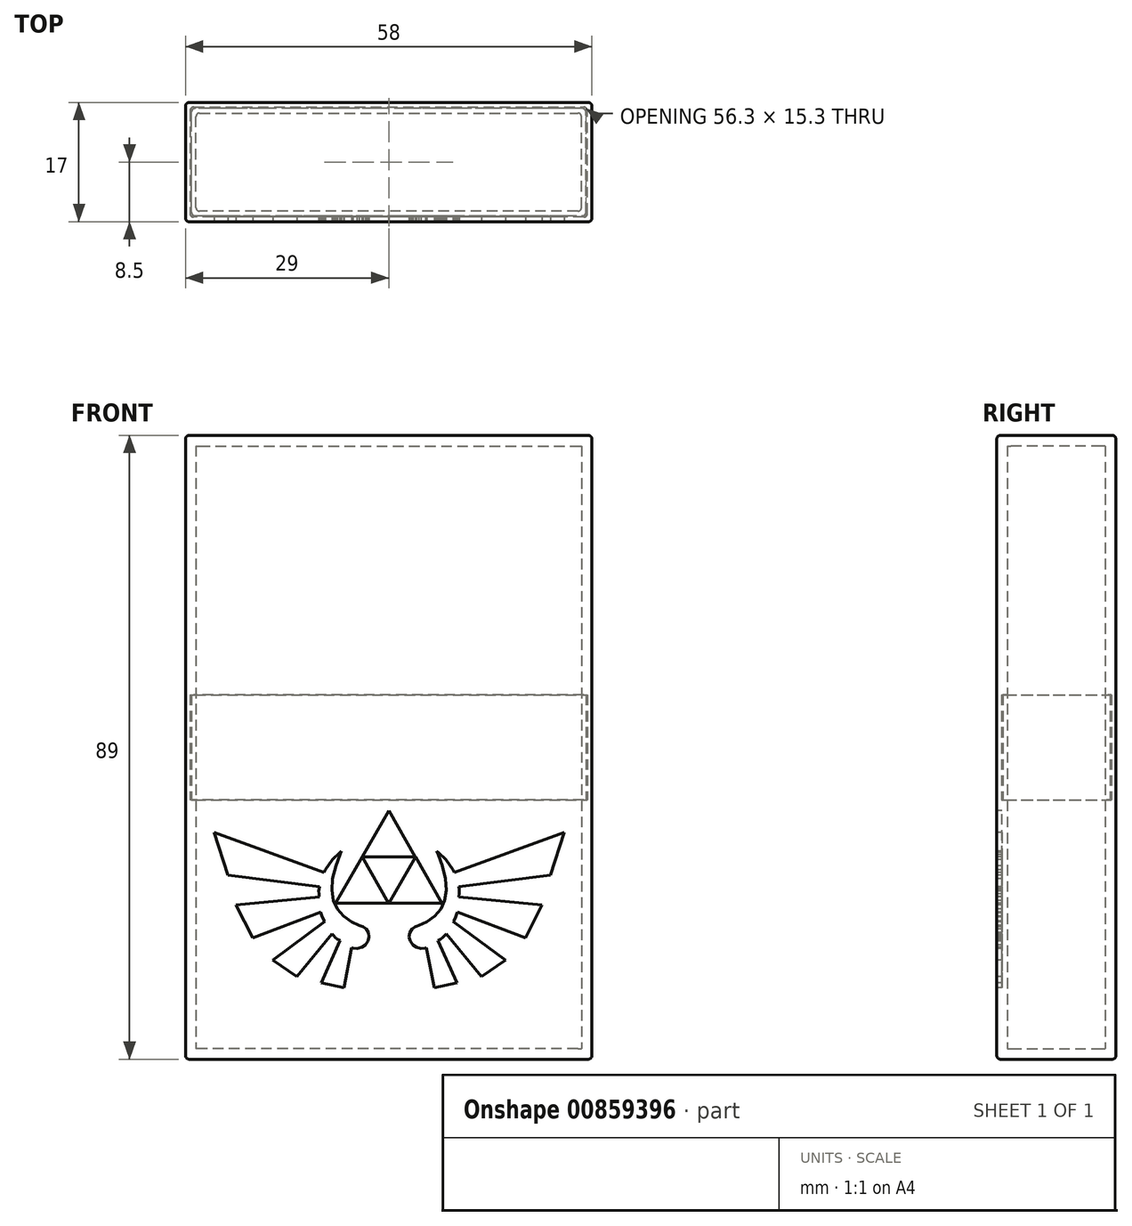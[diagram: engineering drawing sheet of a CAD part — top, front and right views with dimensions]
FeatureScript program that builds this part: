
annotation { "Feature Type Name" : "Feature", "Feature Type Description" : "" }
export const myFeature = defineFeature(function(context is Context, id is Id, definition is map)
    precondition{}
    {
        {
            assignVariable(context, id + "F0", {"name" : "wall_thickness", "anyValue" : 1.5});
        }
        {
            var Q0;
            Q0=qCreatedBy(makeId("Top.planeOp"),FACE);
            var sketch = newSketch(context, id + "F1", { "sketchPlane" : qUnion([Q0])});
            skLineSegment(sketch, "E0", {"start": v(-29, 0) * mm, "end": v(-29, 8.5) * mm});
            skLineSegment(sketch, "E1", {"start": v(-29, 8.5) * mm, "end": v(0, 8.5) * mm});
            skLineSegment(sketch, "E2.MirrorCS", {"start": v(29, 8.5) * mm, "end": v(0, 8.5) * mm});
            skLineSegment(sketch, "E3.MirrorCS", {"start": v(29, 0) * mm, "end": v(29, 8.5) * mm});
            skLineSegment(sketch, "E4.MirrorCS", {"start": v(29, 0) * mm, "end": v(29, -8.5) * mm});
            skLineSegment(sketch, "E5.MirrorCS", {"start": v(29, -8.5) * mm, "end": v(0, -8.5) * mm});
            skLineSegment(sketch, "E6.MirrorCS", {"start": v(-29, -8.5) * mm, "end": v(0, -8.5) * mm});
            skLineSegment(sketch, "E7.MirrorCS", {"start": v(-29, 0) * mm, "end": v(-29, -8.5) * mm});
            skSolve(sketch);
        }
        {
            assignVariable(context, id + "F2", {"name" : "inside_height", "anyValue" : 86});
        }
        {
            var Q0;
            Q0=makeQuery(id+"F1.imprint","IMPRINT",FACE,{"disambiguationData":[TD([[makeQuery(id+"F1.imprint","IMPRINT",EDGE,{"derivedFrom":sQuery(id+"F1.wireOp",EDGE,"E0")}),-1.0]])]});
            extrude(context, id + "F3", {"entities" : qUnion([Q0]), "depth" : (getVariable(context, 'wall_thickness')) * mm, "offsetDistance" : 25 * mm});
        }
        {
            var Q0;
            Q0=makeQuery(id+"F3.opExtrude","CAP_FACE",FACE,{"disambiguationData":[OSD([sQuery(id+"F1.wireOp",EDGE,"E0"),sQuery(id+"F1.wireOp",EDGE,"E1"),sQuery(id+"F1.wireOp",EDGE,"E2.MirrorCS"),sQuery(id+"F1.wireOp",EDGE,"E3.MirrorCS"),sQuery(id+"F1.wireOp",EDGE,"E4.MirrorCS"),sQuery(id+"F1.wireOp",EDGE,"E5.MirrorCS"),sQuery(id+"F1.wireOp",EDGE,"E6.MirrorCS"),sQuery(id+"F1.wireOp",EDGE,"E7.MirrorCS")])],"isStart":false});
            var sketch = newSketch(context, id + "F4", { "sketchPlane" : qUnion([Q0])});
            skLineSegment(sketch, "E8", {"start": v(-27.5, 0) * mm, "end": v(-27.5, 7) * mm});
            skLineSegment(sketch, "E9", {"start": v(-27.5, 7) * mm, "end": v(0, 7) * mm});
            skLineSegment(sketch, "E10.MirrorCS", {"start": v(27.5, 0) * mm, "end": v(27.5, 7) * mm});
            skLineSegment(sketch, "E11.MirrorCS", {"start": v(27.5, 7) * mm, "end": v(0, 7) * mm});
            skLineSegment(sketch, "E12.MirrorCS", {"start": v(27.5, 0) * mm, "end": v(27.5, -7) * mm});
            skLineSegment(sketch, "E13.MirrorCS", {"start": v(27.5, -7) * mm, "end": v(0, -7) * mm});
            skLineSegment(sketch, "E14.MirrorCS", {"start": v(-27.5, -7) * mm, "end": v(0, -7) * mm});
            skLineSegment(sketch, "E15.MirrorCS", {"start": v(-27.5, 0) * mm, "end": v(-27.5, -7) * mm});
            skSolve(sketch);
        }
        {
            assignVariable(context, id + "F5", {"name" : "mate_height", "anyValue" : 15});
        }
        {
            var Q0;
            Q0=makeQuery(id+"F4.imprint","IMPRINT",FACE,{"disambiguationData":[TD([[makeQuery(id+"F4.imprint","IMPRINT",EDGE,{"derivedFrom":sQuery(id+"F4.wireOp",EDGE,"E8")}),1.0]])]});
            extrude(context, id + "F6", {"entities" : qUnion([Q0]), "operationType" : NewBodyOperationType.ADD, "depth" : (getVariable(context, 'inside_height') - getVariable(context, 'mate_height')) / 2 * mm, "offsetDistance" : 25 * mm});
        }
        {
            var Q0;
            Q0=makeQuery(id+"F6.opExtrude","CAP_FACE",FACE,{"disambiguationData":[OSD([sQuery(id+"F1.wireOp",EDGE,"E0"),sQuery(id+"F1.wireOp",EDGE,"E1"),sQuery(id+"F1.wireOp",EDGE,"E2.MirrorCS"),sQuery(id+"F1.wireOp",EDGE,"E3.MirrorCS"),sQuery(id+"F1.wireOp",EDGE,"E4.MirrorCS"),sQuery(id+"F1.wireOp",EDGE,"E5.MirrorCS"),sQuery(id+"F1.wireOp",EDGE,"E6.MirrorCS"),sQuery(id+"F1.wireOp",EDGE,"E7.MirrorCS"),sQuery(id+"F4.wireOp",EDGE,"E8"),sQuery(id+"F4.wireOp",EDGE,"E9"),sQuery(id+"F4.wireOp",EDGE,"E10.MirrorCS"),sQuery(id+"F4.wireOp",EDGE,"E11.MirrorCS"),sQuery(id+"F4.wireOp",EDGE,"E12.MirrorCS"),sQuery(id+"F4.wireOp",EDGE,"E13.MirrorCS"),sQuery(id+"F4.wireOp",EDGE,"E14.MirrorCS"),sQuery(id+"F4.wireOp",EDGE,"E15.MirrorCS")])],"isStart":false});
            var sketch = newSketch(context, id + "F7", { "sketchPlane" : qUnion([Q0])});
            skLineSegment(sketch, "E16", {"start": v(-28.15, 0) * mm, "end": v(-28.15, 7.65) * mm});
            skPoint(sketch, "E16.startSnap0", {"position": v(-29, 0) * mm});
            skLineSegment(sketch, "E17", {"start": v(-28.15, 7.65) * mm, "end": v(0, 7.65) * mm});
            skLineSegment(sketch, "E18.MirrorCS", {"start": v(28.15, 7.65) * mm, "end": v(0, 7.65) * mm});
            skLineSegment(sketch, "E19.MirrorCS", {"start": v(28.15, 0) * mm, "end": v(28.15, 7.65) * mm});
            skLineSegment(sketch, "E20.MirrorCS", {"start": v(-28.15, -7.65) * mm, "end": v(0, -7.65) * mm});
            skLineSegment(sketch, "E21.MirrorCS", {"start": v(28.15, -7.65) * mm, "end": v(0, -7.65) * mm});
            skLineSegment(sketch, "E22.MirrorCS", {"start": v(28.15, 0) * mm, "end": v(28.15, -7.65) * mm});
            skLineSegment(sketch, "E23.MirrorCS", {"start": v(-28.15, 0) * mm, "end": v(-28.15, -7.65) * mm});
            skSolve(sketch);
        }
        {
            var Q0;
            Q0=makeQuery(id+"F6.opExtrude","CAP_FACE",FACE,{"disambiguationData":[OSD([sQuery(id+"F1.wireOp",EDGE,"E0"),sQuery(id+"F1.wireOp",EDGE,"E1"),sQuery(id+"F1.wireOp",EDGE,"E2.MirrorCS"),sQuery(id+"F1.wireOp",EDGE,"E3.MirrorCS"),sQuery(id+"F1.wireOp",EDGE,"E4.MirrorCS"),sQuery(id+"F1.wireOp",EDGE,"E5.MirrorCS"),sQuery(id+"F1.wireOp",EDGE,"E6.MirrorCS"),sQuery(id+"F1.wireOp",EDGE,"E7.MirrorCS"),sQuery(id+"F4.wireOp",EDGE,"E8"),sQuery(id+"F4.wireOp",EDGE,"E9"),sQuery(id+"F4.wireOp",EDGE,"E10.MirrorCS"),sQuery(id+"F4.wireOp",EDGE,"E11.MirrorCS"),sQuery(id+"F4.wireOp",EDGE,"E12.MirrorCS"),sQuery(id+"F4.wireOp",EDGE,"E13.MirrorCS"),sQuery(id+"F4.wireOp",EDGE,"E14.MirrorCS"),sQuery(id+"F4.wireOp",EDGE,"E15.MirrorCS")])],"isStart":false});
            var sketch = newSketch(context, id + "F8", { "sketchPlane" : qUnion([Q0])});
            skLineSegment(sketch, "E24", {"start": v(-28.35, 0) * mm, "end": v(-28.35, 7.85) * mm});
            skPoint(sketch, "E24.startSnap0", {"position": v(-29, 0) * mm});
            skLineSegment(sketch, "E25", {"start": v(-28.35, 7.85) * mm, "end": v(0, 7.85) * mm});
            skLineSegment(sketch, "E26.MirrorCS", {"start": v(28.35, 7.85) * mm, "end": v(0, 7.85) * mm});
            skLineSegment(sketch, "E27.MirrorCS", {"start": v(28.35, 0) * mm, "end": v(28.35, 7.85) * mm});
            skLineSegment(sketch, "E28.MirrorCS", {"start": v(-28.35, -7.85) * mm, "end": v(0, -7.85) * mm});
            skLineSegment(sketch, "E29.MirrorCS", {"start": v(-28.35, 0) * mm, "end": v(-28.35, -7.85) * mm});
            skLineSegment(sketch, "E30.MirrorCS", {"start": v(28.35, -7.85) * mm, "end": v(0, -7.85) * mm});
            skLineSegment(sketch, "E31.MirrorCS", {"start": v(28.35, 0) * mm, "end": v(28.35, -7.85) * mm});
            skSolve(sketch);
        }
        {
            var Q0;
            Q0=makeQuery(id+"F7.imprint","IMPRINT",FACE,{"disambiguationData":[TD([[makeQuery(id+"F7.imprint","IMPRINT",EDGE,{"derivedFrom":sQuery(id+"F7.wireOp",EDGE,"E16")}),-1.0]])]});
            extrude(context, id + "F9", {"entities" : qUnion([Q0]), "operationType" : NewBodyOperationType.ADD, "depth" : (getVariable(context, 'mate_height')) * mm, "offsetDistance" : 25 * mm});
        }
        {
            var Q0;
            Q0=makeQuery(id+"F8.imprint","IMPRINT",FACE,{"disambiguationData":[TD([[makeQuery(id+"F8.imprint","IMPRINT",EDGE,{"derivedFrom":sQuery(id+"F8.wireOp",EDGE,"E24")}),1.0]])]});
            var Q1;
            Q1=makeQuery(id+"F9.opExtrude","CAP_FACE",FACE,{"disambiguationData":[OSD([sQuery(id+"F4.wireOp",EDGE,"E8"),sQuery(id+"F4.wireOp",EDGE,"E9"),sQuery(id+"F4.wireOp",EDGE,"E10.MirrorCS"),sQuery(id+"F4.wireOp",EDGE,"E11.MirrorCS"),sQuery(id+"F4.wireOp",EDGE,"E12.MirrorCS"),sQuery(id+"F4.wireOp",EDGE,"E13.MirrorCS"),sQuery(id+"F4.wireOp",EDGE,"E14.MirrorCS"),sQuery(id+"F4.wireOp",EDGE,"E15.MirrorCS"),sQuery(id+"F7.wireOp",EDGE,"E16"),sQuery(id+"F7.wireOp",EDGE,"E17"),sQuery(id+"F7.wireOp",EDGE,"E18.MirrorCS"),sQuery(id+"F7.wireOp",EDGE,"E19.MirrorCS"),sQuery(id+"F7.wireOp",EDGE,"E20.MirrorCS"),sQuery(id+"F7.wireOp",EDGE,"E21.MirrorCS"),sQuery(id+"F7.wireOp",EDGE,"E22.MirrorCS"),sQuery(id+"F7.wireOp",EDGE,"E23.MirrorCS")])],"isStart":false});
            extrude(context, id + "F10", {"entities" : qUnion([Q0]), "endBound" : BoundingType.UP_TO_SURFACE, "depth" : 25 * mm, "endBoundEntityFace" : qUnion([Q1]), "offsetDistance" : 25 * mm});
        }
        {
            var Q0;
            Q0=makeQuery(id+"F10.opExtrude","CAP_FACE",FACE,{"disambiguationData":[OSD([sQuery(id+"F1.wireOp",EDGE,"E0"),sQuery(id+"F1.wireOp",EDGE,"E1"),sQuery(id+"F1.wireOp",EDGE,"E2.MirrorCS"),sQuery(id+"F1.wireOp",EDGE,"E3.MirrorCS"),sQuery(id+"F1.wireOp",EDGE,"E4.MirrorCS"),sQuery(id+"F1.wireOp",EDGE,"E5.MirrorCS"),sQuery(id+"F1.wireOp",EDGE,"E6.MirrorCS"),sQuery(id+"F1.wireOp",EDGE,"E7.MirrorCS"),sQuery(id+"F8.wireOp",EDGE,"E24"),sQuery(id+"F8.wireOp",EDGE,"E25"),sQuery(id+"F8.wireOp",EDGE,"E26.MirrorCS"),sQuery(id+"F8.wireOp",EDGE,"E27.MirrorCS"),sQuery(id+"F8.wireOp",EDGE,"E28.MirrorCS"),sQuery(id+"F8.wireOp",EDGE,"E29.MirrorCS"),sQuery(id+"F8.wireOp",EDGE,"E30.MirrorCS"),sQuery(id+"F8.wireOp",EDGE,"E31.MirrorCS")])],"isStart":false});
            var sketch = newSketch(context, id + "F11", { "sketchPlane" : qUnion([Q0])});
            skLineSegment(sketch, "E32.bottom", {"start": v(-29, 8.5) * mm, "end": v(29, 8.5) * mm});
            skLineSegment(sketch, "E32.top", {"start": v(-29, -8.5) * mm, "end": v(29, -8.5) * mm});
            skLineSegment(sketch, "E32.left", {"start": v(-29, 8.5) * mm, "end": v(-29, -8.5) * mm});
            skLineSegment(sketch, "E32.right", {"start": v(29, 8.5) * mm, "end": v(29, -8.5) * mm});
            skLineSegment(sketch, "E33.bottom", {"start": v(-27.5, 7) * mm, "end": v(27.5, 7) * mm});
            skLineSegment(sketch, "E33.top", {"start": v(-27.5, -7) * mm, "end": v(27.5, -7) * mm});
            skLineSegment(sketch, "E33.left", {"start": v(-27.5, 7) * mm, "end": v(-27.5, -7) * mm});
            skLineSegment(sketch, "E33.right", {"start": v(27.5, 7) * mm, "end": v(27.5, -7) * mm});
            skSolve(sketch);
        }
        {
            var Q0;
            Q0 = qSketchRegion(id + "F11", true);
            extrude(context, id + "F12", {"entities" : qUnion([Q0]), "operationType" : NewBodyOperationType.ADD, "depth" : (getVariable(context, 'inside_height') - getVariable(context, 'mate_height')) / 2 * mm, "offsetDistance" : 25 * mm});
        }
        {
            var Q0;
            Q0=makeQuery(id+"F12.opExtrude","CAP_FACE",FACE,{"disambiguationData":[OSD([sQuery(id+"F11.wireOp",EDGE,"E32.bottom"),sQuery(id+"F11.wireOp",EDGE,"E32.top"),sQuery(id+"F11.wireOp",EDGE,"E32.left"),sQuery(id+"F11.wireOp",EDGE,"E32.right"),sQuery(id+"F11.wireOp",EDGE,"E33.bottom"),sQuery(id+"F11.wireOp",EDGE,"E33.top"),sQuery(id+"F11.wireOp",EDGE,"E33.left"),sQuery(id+"F11.wireOp",EDGE,"E33.right")])],"isStart":false});
            var sketch = newSketch(context, id + "F13", { "sketchPlane" : qUnion([Q0])});
            skLineSegment(sketch, "E34.bottom", {"start": v(-29, 8.5) * mm, "end": v(29, 8.5) * mm});
            skLineSegment(sketch, "E34.top", {"start": v(-29, -8.5) * mm, "end": v(29, -8.5) * mm});
            skLineSegment(sketch, "E34.left", {"start": v(-29, 8.5) * mm, "end": v(-29, -8.5) * mm});
            skLineSegment(sketch, "E34.right", {"start": v(29, 8.5) * mm, "end": v(29, -8.5) * mm});
            skSolve(sketch);
        }
        {
            var Q0;
            Q0 = qSketchRegion(id + "F13", true);
            extrude(context, id + "F14", {"entities" : qUnion([Q0]), "operationType" : NewBodyOperationType.ADD, "depth" : (getVariable(context, 'wall_thickness')) * mm, "offsetDistance" : 25 * mm});
        }
        {
            var Q0;
            {var subQ0=sQuery(id+"F1.wireOp",EDGE,"E7.MirrorCS");var subQ1=sQuery(id+"F1.wireOp",EDGE,"E6.MirrorCS");Q0=makeQuery(id+"F6.boolean.opBoolean","MERGE",EDGE,{"derivedFrom":[makeQuery(id+"F3.opExtrude","SWEPT_EDGE",EDGE,{"disambiguationData":[OSD([subQ1,subQ0])]}),makeQuery(id+"F6.opExtrude","SWEPT_EDGE",EDGE,{"disambiguationData":[OSD([sQuery(id+"F1.wireOp",EDGE,"E0"),sQuery(id+"F1.wireOp",EDGE,"E5.MirrorCS"),subQ1,subQ0])]})]});}
            var Q1;
            {var subQ0=sQuery(id+"F1.wireOp",EDGE,"E1");var subQ1=sQuery(id+"F1.wireOp",EDGE,"E0");Q1=makeQuery(id+"F6.boolean.opBoolean","MERGE",EDGE,{"derivedFrom":[makeQuery(id+"F3.opExtrude","SWEPT_EDGE",EDGE,{"disambiguationData":[OSD([subQ1,subQ0])]}),makeQuery(id+"F6.opExtrude","SWEPT_EDGE",EDGE,{"disambiguationData":[OSD([subQ1,subQ0,sQuery(id+"F1.wireOp",EDGE,"E2.MirrorCS"),sQuery(id+"F1.wireOp",EDGE,"E7.MirrorCS")])]})]});}
            var Q2;
            {var subQ0=sQuery(id+"F1.wireOp",EDGE,"E3.MirrorCS");var subQ1=sQuery(id+"F1.wireOp",EDGE,"E2.MirrorCS");Q2=makeQuery(id+"F6.boolean.opBoolean","MERGE",EDGE,{"derivedFrom":[makeQuery(id+"F3.opExtrude","SWEPT_EDGE",EDGE,{"disambiguationData":[OSD([subQ1,subQ0])]}),makeQuery(id+"F6.opExtrude","SWEPT_EDGE",EDGE,{"disambiguationData":[OSD([sQuery(id+"F1.wireOp",EDGE,"E1"),subQ1,subQ0,sQuery(id+"F1.wireOp",EDGE,"E4.MirrorCS")])]})]});}
            var Q3;
            {var subQ0=sQuery(id+"F1.wireOp",EDGE,"E5.MirrorCS");var subQ1=sQuery(id+"F1.wireOp",EDGE,"E4.MirrorCS");Q3=makeQuery(id+"F6.boolean.opBoolean","MERGE",EDGE,{"derivedFrom":[makeQuery(id+"F3.opExtrude","SWEPT_EDGE",EDGE,{"disambiguationData":[OSD([subQ1,subQ0])]}),makeQuery(id+"F6.opExtrude","SWEPT_EDGE",EDGE,{"disambiguationData":[OSD([sQuery(id+"F1.wireOp",EDGE,"E3.MirrorCS"),subQ1,subQ0,sQuery(id+"F1.wireOp",EDGE,"E6.MirrorCS")])]})]});}
            var Q4;
            Q4=makeQuery(id+"F9.opExtrude","SWEPT_EDGE",EDGE,{"disambiguationData":[OSD([sQuery(id+"F7.wireOp",EDGE,"E21.MirrorCS"),sQuery(id+"F7.wireOp",EDGE,"E22.MirrorCS")])]});
            var Q5;
            Q5=makeQuery(id+"F9.opExtrude","SWEPT_EDGE",EDGE,{"disambiguationData":[OSD([sQuery(id+"F7.wireOp",EDGE,"E18.MirrorCS"),sQuery(id+"F7.wireOp",EDGE,"E19.MirrorCS")])]});
            var Q6;
            Q6=makeQuery(id+"F9.opExtrude","SWEPT_EDGE",EDGE,{"disambiguationData":[OSD([sQuery(id+"F7.wireOp",EDGE,"E16"),sQuery(id+"F7.wireOp",EDGE,"E17")])]});
            var Q7;
            Q7=makeQuery(id+"F9.opExtrude","SWEPT_EDGE",EDGE,{"disambiguationData":[OSD([sQuery(id+"F7.wireOp",EDGE,"E20.MirrorCS"),sQuery(id+"F7.wireOp",EDGE,"E23.MirrorCS")])]});
            var Q8;
            {var subQ0=sQuery(id+"F4.wireOp",EDGE,"E11.MirrorCS");var subQ1=sQuery(id+"F4.wireOp",EDGE,"E10.MirrorCS");Q8=makeQuery(id+"F9.boolean.opBoolean","MERGE",EDGE,{"derivedFrom":[makeQuery(id+"F6.opExtrude","SWEPT_EDGE",EDGE,{"disambiguationData":[OSD([subQ1,subQ0])]}),makeQuery(id+"F9.opExtrude","SWEPT_EDGE",EDGE,{"disambiguationData":[OSD([sQuery(id+"F4.wireOp",EDGE,"E9"),subQ1,subQ0,sQuery(id+"F4.wireOp",EDGE,"E12.MirrorCS")])]})]});}
            var Q9;
            {var subQ0=sQuery(id+"F4.wireOp",EDGE,"E9");var subQ1=sQuery(id+"F4.wireOp",EDGE,"E8");Q9=makeQuery(id+"F9.boolean.opBoolean","MERGE",EDGE,{"derivedFrom":[makeQuery(id+"F6.opExtrude","SWEPT_EDGE",EDGE,{"disambiguationData":[OSD([subQ1,subQ0])]}),makeQuery(id+"F9.opExtrude","SWEPT_EDGE",EDGE,{"disambiguationData":[OSD([subQ1,subQ0,sQuery(id+"F4.wireOp",EDGE,"E11.MirrorCS"),sQuery(id+"F4.wireOp",EDGE,"E15.MirrorCS")])]})]});}
            var Q10;
            {var subQ0=sQuery(id+"F4.wireOp",EDGE,"E15.MirrorCS");var subQ1=sQuery(id+"F4.wireOp",EDGE,"E14.MirrorCS");Q10=makeQuery(id+"F9.boolean.opBoolean","MERGE",EDGE,{"derivedFrom":[makeQuery(id+"F6.opExtrude","SWEPT_EDGE",EDGE,{"disambiguationData":[OSD([subQ1,subQ0])]}),makeQuery(id+"F9.opExtrude","SWEPT_EDGE",EDGE,{"disambiguationData":[OSD([sQuery(id+"F4.wireOp",EDGE,"E8"),sQuery(id+"F4.wireOp",EDGE,"E13.MirrorCS"),subQ1,subQ0])]})]});}
            var Q11;
            {var subQ0=sQuery(id+"F4.wireOp",EDGE,"E13.MirrorCS");var subQ1=sQuery(id+"F4.wireOp",EDGE,"E12.MirrorCS");Q11=makeQuery(id+"F9.boolean.opBoolean","MERGE",EDGE,{"derivedFrom":[makeQuery(id+"F6.opExtrude","SWEPT_EDGE",EDGE,{"disambiguationData":[OSD([subQ1,subQ0])]}),makeQuery(id+"F9.opExtrude","SWEPT_EDGE",EDGE,{"disambiguationData":[OSD([sQuery(id+"F4.wireOp",EDGE,"E10.MirrorCS"),subQ1,subQ0,sQuery(id+"F4.wireOp",EDGE,"E14.MirrorCS")])]})]});}
            var Q12;
            Q12=makeQuery(id+"F14.boolean.opBoolean","MERGE",EDGE,{"derivedFrom":[makeQuery(id+"F12.boolean.opBoolean","MERGE",EDGE,{"derivedFrom":[makeQuery(id+"F10.opExtrude","SWEPT_EDGE",EDGE,{"disambiguationData":[OSD([sQuery(id+"F1.wireOp",EDGE,"E0"),sQuery(id+"F1.wireOp",EDGE,"E5.MirrorCS"),sQuery(id+"F1.wireOp",EDGE,"E6.MirrorCS"),sQuery(id+"F1.wireOp",EDGE,"E7.MirrorCS")])]}),makeQuery(id+"F12.opExtrude","SWEPT_EDGE",EDGE,{"disambiguationData":[OSD([sQuery(id+"F11.wireOp",EDGE,"E32.top"),sQuery(id+"F11.wireOp",EDGE,"E32.left")])]})]}),makeQuery(id+"F14.opExtrude","SWEPT_EDGE",EDGE,{"disambiguationData":[OSD([sQuery(id+"F13.wireOp",EDGE,"E34.top"),sQuery(id+"F13.wireOp",EDGE,"E34.left")])]})]});
            var Q13;
            Q13=makeQuery(id+"F14.boolean.opBoolean","MERGE",EDGE,{"derivedFrom":[makeQuery(id+"F12.boolean.opBoolean","MERGE",EDGE,{"derivedFrom":[makeQuery(id+"F10.opExtrude","SWEPT_EDGE",EDGE,{"disambiguationData":[OSD([sQuery(id+"F1.wireOp",EDGE,"E0"),sQuery(id+"F1.wireOp",EDGE,"E1"),sQuery(id+"F1.wireOp",EDGE,"E2.MirrorCS"),sQuery(id+"F1.wireOp",EDGE,"E7.MirrorCS")])]}),makeQuery(id+"F12.opExtrude","SWEPT_EDGE",EDGE,{"disambiguationData":[OSD([sQuery(id+"F11.wireOp",EDGE,"E32.bottom"),sQuery(id+"F11.wireOp",EDGE,"E32.left")])]})]}),makeQuery(id+"F14.opExtrude","SWEPT_EDGE",EDGE,{"disambiguationData":[OSD([sQuery(id+"F13.wireOp",EDGE,"E34.bottom"),sQuery(id+"F13.wireOp",EDGE,"E34.left")])]})]});
            var Q14;
            Q14=makeQuery(id+"F14.boolean.opBoolean","MERGE",EDGE,{"derivedFrom":[makeQuery(id+"F12.boolean.opBoolean","MERGE",EDGE,{"derivedFrom":[makeQuery(id+"F10.opExtrude","SWEPT_EDGE",EDGE,{"disambiguationData":[OSD([sQuery(id+"F1.wireOp",EDGE,"E3.MirrorCS"),sQuery(id+"F1.wireOp",EDGE,"E4.MirrorCS"),sQuery(id+"F1.wireOp",EDGE,"E5.MirrorCS"),sQuery(id+"F1.wireOp",EDGE,"E6.MirrorCS")])]}),makeQuery(id+"F12.opExtrude","SWEPT_EDGE",EDGE,{"disambiguationData":[OSD([sQuery(id+"F11.wireOp",EDGE,"E32.top"),sQuery(id+"F11.wireOp",EDGE,"E32.right")])]})]}),makeQuery(id+"F14.opExtrude","SWEPT_EDGE",EDGE,{"disambiguationData":[OSD([sQuery(id+"F13.wireOp",EDGE,"E34.top"),sQuery(id+"F13.wireOp",EDGE,"E34.right")])]})]});
            var Q15;
            Q15=makeQuery(id+"F14.boolean.opBoolean","MERGE",EDGE,{"derivedFrom":[makeQuery(id+"F12.boolean.opBoolean","MERGE",EDGE,{"derivedFrom":[makeQuery(id+"F10.opExtrude","SWEPT_EDGE",EDGE,{"disambiguationData":[OSD([sQuery(id+"F1.wireOp",EDGE,"E1"),sQuery(id+"F1.wireOp",EDGE,"E2.MirrorCS"),sQuery(id+"F1.wireOp",EDGE,"E3.MirrorCS"),sQuery(id+"F1.wireOp",EDGE,"E4.MirrorCS")])]}),makeQuery(id+"F12.opExtrude","SWEPT_EDGE",EDGE,{"disambiguationData":[OSD([sQuery(id+"F11.wireOp",EDGE,"E32.bottom"),sQuery(id+"F11.wireOp",EDGE,"E32.right")])]})]}),makeQuery(id+"F14.opExtrude","SWEPT_EDGE",EDGE,{"disambiguationData":[OSD([sQuery(id+"F13.wireOp",EDGE,"E34.bottom"),sQuery(id+"F13.wireOp",EDGE,"E34.right")])]})]});
            var Q16;
            Q16=makeQuery(id+"F10.opExtrude","SWEPT_EDGE",EDGE,{"disambiguationData":[OSD([sQuery(id+"F8.wireOp",EDGE,"E28.MirrorCS"),sQuery(id+"F8.wireOp",EDGE,"E29.MirrorCS")])]});
            var Q17;
            Q17=makeQuery(id+"F10.opExtrude","SWEPT_EDGE",EDGE,{"disambiguationData":[OSD([sQuery(id+"F8.wireOp",EDGE,"E24"),sQuery(id+"F8.wireOp",EDGE,"E25")])]});
            var Q18;
            Q18=makeQuery(id+"F10.opExtrude","SWEPT_EDGE",EDGE,{"disambiguationData":[OSD([sQuery(id+"F8.wireOp",EDGE,"E26.MirrorCS"),sQuery(id+"F8.wireOp",EDGE,"E27.MirrorCS")])]});
            var Q19;
            Q19=makeQuery(id+"F10.opExtrude","SWEPT_EDGE",EDGE,{"disambiguationData":[OSD([sQuery(id+"F8.wireOp",EDGE,"E30.MirrorCS"),sQuery(id+"F8.wireOp",EDGE,"E31.MirrorCS")])]});
            var Q20;
            Q20=makeQuery(id+"F12.opExtrude","SWEPT_EDGE",EDGE,{"disambiguationData":[OSD([sQuery(id+"F11.wireOp",EDGE,"E33.top"),sQuery(id+"F11.wireOp",EDGE,"E33.right")])]});
            var Q21;
            Q21=makeQuery(id+"F12.opExtrude","SWEPT_EDGE",EDGE,{"disambiguationData":[OSD([sQuery(id+"F11.wireOp",EDGE,"E33.bottom"),sQuery(id+"F11.wireOp",EDGE,"E33.right")])]});
            var Q22;
            Q22=makeQuery(id+"F12.opExtrude","SWEPT_EDGE",EDGE,{"disambiguationData":[OSD([sQuery(id+"F11.wireOp",EDGE,"E33.top"),sQuery(id+"F11.wireOp",EDGE,"E33.left")])]});
            var Q23;
            Q23=makeQuery(id+"F12.opExtrude","SWEPT_EDGE",EDGE,{"disambiguationData":[OSD([sQuery(id+"F11.wireOp",EDGE,"E33.bottom"),sQuery(id+"F11.wireOp",EDGE,"E33.left")])]});
            var Q24;
            Q24=makeQuery(id+"F14.opExtrude","CAP_FACE",FACE,{"disambiguationData":[OSD([sQuery(id+"F13.wireOp",EDGE,"E34.bottom"),sQuery(id+"F13.wireOp",EDGE,"E34.top"),sQuery(id+"F13.wireOp",EDGE,"E34.left"),sQuery(id+"F13.wireOp",EDGE,"E34.right")])],"isStart":false});
            var Q25;
            Q25=makeQuery(id+"F3.opExtrude","CAP_FACE",FACE,{"disambiguationData":[OSD([sQuery(id+"F1.wireOp",EDGE,"E0"),sQuery(id+"F1.wireOp",EDGE,"E1"),sQuery(id+"F1.wireOp",EDGE,"E2.MirrorCS"),sQuery(id+"F1.wireOp",EDGE,"E3.MirrorCS"),sQuery(id+"F1.wireOp",EDGE,"E4.MirrorCS"),sQuery(id+"F1.wireOp",EDGE,"E5.MirrorCS"),sQuery(id+"F1.wireOp",EDGE,"E6.MirrorCS"),sQuery(id+"F1.wireOp",EDGE,"E7.MirrorCS")])],"isStart":true});
            fillet(context, id + "F15", {"entities" : qUnion([Q0, Q1, Q2, Q3, Q4, Q5, Q6, Q7, Q8, Q9, Q10, Q11, Q12, Q13, Q14, Q15, Q16, Q17, Q18, Q19, Q20, Q21, Q22, Q23, Q24, Q25]), "radius" : .5 * mm, "tangentPropagation" : true, "allowEdgeOverflow" : false});
        }
        {
            var Q0;
            {var subQ0=sQuery(id+"F1.wireOp",EDGE,"E6.MirrorCS");var subQ1=sQuery(id+"F1.wireOp",EDGE,"E5.MirrorCS");Q0=makeQuery(id+"F6.boolean.opBoolean","MERGE",FACE,{"derivedFrom":[makeQuery(id+"F3.opExtrude","SWEPT_FACE",FACE,{"disambiguationData":[OSD([subQ1,subQ0])]}),makeQuery(id+"F6.opExtrude","SWEPT_FACE",FACE,{"disambiguationData":[OSD([subQ1,subQ0])]})]});}
            var sketch = newSketch(context, id + "F16", { "sketchPlane" : qUnion([Q0])});
            skLineSegment(sketch, "E35", {"start": v(-22.97, 26.26) * mm, "end": v(-9.88, 24.62) * mm});
            skLineSegment(sketch, "E36", {"start": v(-9.88, 24.62) * mm, "end": v(-9.9, 24.54) * mm});
            skLineSegment(sketch, "E37", {"start": v(-9.9, 24.54) * mm, "end": v(-9.94, 24.3) * mm});
            skLineSegment(sketch, "E38", {"start": v(-9.94, 24.3) * mm, "end": v(-9.98, 23.95) * mm});
            skLineSegment(sketch, "E39", {"start": v(-9.98, 23.95) * mm, "end": v(-9.97, 23.57) * mm});
            skLineSegment(sketch, "E40", {"start": v(-9.97, 23.57) * mm, "end": v(-9.91, 23.23) * mm});
            skLineSegment(sketch, "E41", {"start": v(-9.91, 23.23) * mm, "end": v(-9.88, 23.12) * mm});
            skLineSegment(sketch, "E42", {"start": v(-9.88, 23.12) * mm, "end": v(-21.81, 22.01) * mm});
            skLineSegment(sketch, "E43", {"start": v(-21.81, 22.01) * mm, "end": v(-19.4, 17.32) * mm});
            skLineSegment(sketch, "E44", {"start": v(-19.4, 17.32) * mm, "end": v(-9.69, 21) * mm});
            skLineSegment(sketch, "E45", {"start": v(-9.69, 21) * mm, "end": v(-9.66, 20.87) * mm});
            skLineSegment(sketch, "E46", {"start": v(-9.66, 20.87) * mm, "end": v(-9.46, 20.27) * mm});
            skLineSegment(sketch, "E47", {"start": v(-9.46, 20.27) * mm, "end": v(-9.18, 19.74) * mm});
            skLineSegment(sketch, "E48", {"start": v(-9.18, 19.74) * mm, "end": v(-9.1, 19.64) * mm});
            skLineSegment(sketch, "E49", {"start": v(-9.1, 19.64) * mm, "end": v(-16.55, 14.14) * mm});
            skLineSegment(sketch, "E50", {"start": v(-16.55, 14.14) * mm, "end": v(-13.12, 11.82) * mm});
            skLineSegment(sketch, "E51", {"start": v(-13.12, 11.82) * mm, "end": v(-8.1, 17.86) * mm});
            skLineSegment(sketch, "E52", {"start": v(-8.1, 17.86) * mm, "end": v(-8.03, 17.8) * mm});
            skLineSegment(sketch, "E53", {"start": v(-8.03, 17.8) * mm, "end": v(-7.87, 17.6) * mm});
            skLineSegment(sketch, "E54", {"start": v(-7.87, 17.6) * mm, "end": v(-7.63, 17.35) * mm});
            skLineSegment(sketch, "E55", {"start": v(-7.63, 17.35) * mm, "end": v(-7.33, 17.12) * mm});
            skLineSegment(sketch, "E56", {"start": v(-7.33, 17.12) * mm, "end": v(-7.04, 16.97) * mm});
            skLineSegment(sketch, "E57", {"start": v(-7.04, 16.97) * mm, "end": v(-6.93, 16.94) * mm});
            skLineSegment(sketch, "E58", {"start": v(-6.93, 16.94) * mm, "end": v(-9.64, 10.9) * mm});
            skLineSegment(sketch, "E59", {"start": v(-9.64, 10.9) * mm, "end": v(-6.4, 10.18) * mm});
            skLineSegment(sketch, "E60", {"start": v(-6.4, 10.18) * mm, "end": v(-5.3, 15.92) * mm});
            skLineSegment(sketch, "E61", {"start": v(-5.3, 15.92) * mm, "end": v(-5.11, 15.86) * mm});
            skLineSegment(sketch, "E62", {"start": v(-5.11, 15.86) * mm, "end": v(-4.52, 15.79) * mm});
            skLineSegment(sketch, "E63", {"start": v(-4.52, 15.79) * mm, "end": v(-3.86, 15.95) * mm});
            skLineSegment(sketch, "E64", {"start": v(-3.86, 15.95) * mm, "end": v(-3.34, 16.32) * mm});
            skLineSegment(sketch, "E65", {"start": v(-3.34, 16.32) * mm, "end": v(-2.98, 16.85) * mm});
            skLineSegment(sketch, "E66", {"start": v(-2.98, 16.85) * mm, "end": v(-2.82, 17.45) * mm});
            skLineSegment(sketch, "E67", {"start": v(-2.82, 17.45) * mm, "end": v(-2.9, 18.05) * mm});
            skLineSegment(sketch, "E68", {"start": v(-2.9, 18.05) * mm, "end": v(-3.22, 18.58) * mm});
            skLineSegment(sketch, "E69", {"start": v(-3.22, 18.58) * mm, "end": v(-3.67, 18.9) * mm});
            skLineSegment(sketch, "E70", {"start": v(-3.67, 18.9) * mm, "end": v(-3.84, 18.97) * mm});
            skLineSegment(sketch, "E71", {"start": v(-3.84, 18.97) * mm, "end": v(-4.22, 19.1) * mm});
            skLineSegment(sketch, "E72", {"start": v(-4.22, 19.1) * mm, "end": v(-5.3, 19.6) * mm});
            skLineSegment(sketch, "E73", {"start": v(-5.3, 19.6) * mm, "end": v(-6.47, 20.42) * mm});
            skLineSegment(sketch, "E74", {"start": v(-6.47, 20.42) * mm, "end": v(-7.33, 21.44) * mm});
            skLineSegment(sketch, "E75", {"start": v(-7.33, 21.44) * mm, "end": v(-7.89, 22.66) * mm});
            skLineSegment(sketch, "E76", {"start": v(-7.89, 22.66) * mm, "end": v(-8.11, 24.08) * mm});
            skLineSegment(sketch, "E77", {"start": v(-8.11, 24.08) * mm, "end": v(-8, 25.73) * mm});
            skLineSegment(sketch, "E78", {"start": v(-8, 25.73) * mm, "end": v(-7.55, 27.6) * mm});
            skLineSegment(sketch, "E79", {"start": v(-7.55, 27.6) * mm, "end": v(-6.97, 29.18) * mm});
            skLineSegment(sketch, "E80", {"start": v(-6.97, 29.18) * mm, "end": v(-6.74, 29.7) * mm});
            skLineSegment(sketch, "E81", {"start": v(-6.74, 29.7) * mm, "end": v(-6.97, 29.52) * mm});
            skLineSegment(sketch, "E82", {"start": v(-6.97, 29.52) * mm, "end": v(-8.06, 28.5) * mm});
            skLineSegment(sketch, "E83", {"start": v(-8.06, 28.5) * mm, "end": v(-9.07, 27.03) * mm});
            skLineSegment(sketch, "E84", {"start": v(-9.07, 27.03) * mm, "end": v(-9.25, 26.65) * mm});
            skLineSegment(sketch, "E85", {"start": v(-9.25, 26.65) * mm, "end": v(-24.95, 32.35) * mm});
            skLineSegment(sketch, "E86", {"start": v(-24.95, 32.35) * mm, "end": v(-22.97, 26.26) * mm});
            skLineSegment(sketch, "E87", {"start": v(-7.6, 22.3) * mm, "end": v(0, 22.3) * mm});
            skLineSegment(sketch, "E88", {"start": v(3.8, 28.88) * mm, "end": v(0, 35.47) * mm});
            skLineSegment(sketch, "E89", {"start": v(0, 22.3) * mm, "end": v(7.6, 22.3) * mm});
            skLineSegment(sketch, "E90", {"start": v(7.6, 22.3) * mm, "end": v(3.8, 28.88) * mm});
            skLineSegment(sketch, "E91", {"start": v(-5, 5.2) * mm, "end": v(-4.52, 6.82) * mm});
            skLineSegment(sketch, "E92", {"start": v(-4.52, 6.82) * mm, "end": v(-7.37, 6.82) * mm});
            skLineSegment(sketch, "E93", {"start": v(-7.37, 6.82) * mm, "end": v(-6.55, 4.62) * mm});
            skLineSegment(sketch, "E94", {"start": v(-6.55, 4.62) * mm, "end": v(-9.5, 6.94) * mm});
            skLineSegment(sketch, "E95", {"start": v(-9.5, 6.94) * mm, "end": v(-9.58, 7.01) * mm});
            skLineSegment(sketch, "E96", {"start": v(-9.58, 7.01) * mm, "end": v(-9.82, 7.28) * mm});
            skLineSegment(sketch, "E97", {"start": v(-9.82, 7.28) * mm, "end": v(-9.92, 7.58) * mm});
            skLineSegment(sketch, "E98", {"start": v(-9.92, 7.58) * mm, "end": v(-9.77, 7.79) * mm});
            skLineSegment(sketch, "E99", {"start": v(-9.77, 7.79) * mm, "end": v(-9.45, 7.86) * mm});
            skLineSegment(sketch, "E100", {"start": v(-9.45, 7.86) * mm, "end": v(-9.35, 7.86) * mm});
            skLineSegment(sketch, "E101", {"start": v(-9.35, 7.86) * mm, "end": v(-5.53, 7.86) * mm});
            skLineSegment(sketch, "E102", {"start": v(-5.53, 7.86) * mm, "end": v(-4.03, 11.14) * mm});
            skLineSegment(sketch, "E103", {"start": v(-4.03, 11.14) * mm, "end": v(-4, 11.22) * mm});
            skLineSegment(sketch, "E104", {"start": v(-4, 11.22) * mm, "end": v(-3.8, 11.44) * mm});
            skLineSegment(sketch, "E105", {"start": v(-3.8, 11.44) * mm, "end": v(-3.5, 11.6) * mm});
            skLineSegment(sketch, "E106", {"start": v(-3.5, 11.6) * mm, "end": v(-3.18, 11.64) * mm});
            skLineSegment(sketch, "E107", {"start": v(-3.18, 11.64) * mm, "end": v(-2.86, 11.56) * mm});
            skLineSegment(sketch, "E108", {"start": v(-2.86, 11.56) * mm, "end": v(-2.59, 11.39) * mm});
            skLineSegment(sketch, "E109", {"start": v(-2.59, 11.39) * mm, "end": v(-2.4, 11.12) * mm});
            skLineSegment(sketch, "E110", {"start": v(-2.4, 11.12) * mm, "end": v(-2.36, 10.78) * mm});
            skLineSegment(sketch, "E111", {"start": v(-2.36, 10.78) * mm, "end": v(-2.44, 10.46) * mm});
            skLineSegment(sketch, "E112", {"start": v(-2.44, 10.46) * mm, "end": v(-2.49, 10.37) * mm});
            skLineSegment(sketch, "E113", {"start": v(-2.49, 10.37) * mm, "end": v(-4.08, 7.86) * mm});
            skLineSegment(sketch, "E114", {"start": v(-4.08, 7.86) * mm, "end": v(-3.36, 7.86) * mm});
            skLineSegment(sketch, "E115", {"start": v(-3.36, 7.86) * mm, "end": v(-3.27, 7.86) * mm});
            skLineSegment(sketch, "E116", {"start": v(-3.27, 7.86) * mm, "end": v(-3, 7.77) * mm});
            skLineSegment(sketch, "E117", {"start": v(-3, 7.77) * mm, "end": v(-2.84, 7.54) * mm});
            skLineSegment(sketch, "E118", {"start": v(-2.84, 7.54) * mm, "end": v(-2.87, 7.24) * mm});
            skLineSegment(sketch, "E119", {"start": v(-2.87, 7.24) * mm, "end": v(-3, 7) * mm});
            skLineSegment(sketch, "E120", {"start": v(-3, 7) * mm, "end": v(-3.07, 6.94) * mm});
            skLineSegment(sketch, "E121", {"start": v(-3.07, 6.94) * mm, "end": v(-5, 5.2) * mm});
            skLineSegment(sketch, "E122", {"start": v(-0.02, 4.48) * mm, "end": v(-1.72, 9.05) * mm});
            skLineSegment(sketch, "E123", {"start": v(-1.72, 9.05) * mm, "end": v(-1.64, 9.16) * mm});
            skLineSegment(sketch, "E124", {"start": v(-1.64, 9.16) * mm, "end": v(-1.46, 9.53) * mm});
            skLineSegment(sketch, "E125", {"start": v(-1.46, 9.53) * mm, "end": v(-1.27, 10.14) * mm});
            skLineSegment(sketch, "E126", {"start": v(-1.27, 10.14) * mm, "end": v(-1.16, 10.9) * mm});
            skLineSegment(sketch, "E127", {"start": v(-1.16, 10.9) * mm, "end": v(-1.13, 11.63) * mm});
            skLineSegment(sketch, "E128", {"start": v(-1.13, 11.63) * mm, "end": v(-1.14, 11.87) * mm});
            skLineSegment(sketch, "E129", {"start": v(-1.14, 11.87) * mm, "end": v(-1.26, 12.04) * mm});
            skLineSegment(sketch, "E130", {"start": v(-1.26, 12.04) * mm, "end": v(-1.71, 12.5) * mm});
            skLineSegment(sketch, "E131", {"start": v(-1.71, 12.5) * mm, "end": v(-2.33, 12.97) * mm});
            skLineSegment(sketch, "E132", {"start": v(-2.33, 12.97) * mm, "end": v(-2.98, 13.34) * mm});
            skLineSegment(sketch, "E133", {"start": v(-2.98, 13.34) * mm, "end": v(-3.48, 13.6) * mm});
            skLineSegment(sketch, "E134", {"start": v(-3.48, 13.6) * mm, "end": v(-3.65, 13.68) * mm});
            skLineSegment(sketch, "E135", {"start": v(-3.65, 13.68) * mm, "end": v(-3.52, 13.8) * mm});
            skLineSegment(sketch, "E136", {"start": v(-3.52, 13.8) * mm, "end": v(-3.13, 14.18) * mm});
            skLineSegment(sketch, "E137", {"start": v(-3.13, 14.18) * mm, "end": v(-2.64, 14.73) * mm});
            skLineSegment(sketch, "E138", {"start": v(-2.64, 14.73) * mm, "end": v(-2.25, 15.37) * mm});
            skLineSegment(sketch, "E139", {"start": v(-2.25, 15.37) * mm, "end": v(-2.04, 15.93) * mm});
            skLineSegment(sketch, "E140", {"start": v(-2.04, 15.93) * mm, "end": v(-2, 16.13) * mm});
            skLineSegment(sketch, "E141", {"start": v(-2, 16.13) * mm, "end": v(-1.97, 16.3) * mm});
            skLineSegment(sketch, "E142", {"start": v(-1.97, 16.3) * mm, "end": v(-1.83, 16.83) * mm});
            skLineSegment(sketch, "E143", {"start": v(-1.83, 16.83) * mm, "end": v(-1.56, 17.47) * mm});
            skLineSegment(sketch, "E144", {"start": v(-1.56, 17.47) * mm, "end": v(-1.21, 18.06) * mm});
            skLineSegment(sketch, "E145", {"start": v(-1.21, 18.06) * mm, "end": v(-0.9, 18.47) * mm});
            skLineSegment(sketch, "E146", {"start": v(-0.9, 18.47) * mm, "end": v(-0.8, 18.6) * mm});
            skLineSegment(sketch, "E147", {"start": v(-0.8, 18.6) * mm, "end": v(-0.02, 20.85) * mm});
            skLineSegment(sketch, "E148", {"start": v(-0.02, 20.85) * mm, "end": v(0.7, 18.6) * mm});
            skLineSegment(sketch, "E149", {"start": v(0.7, 18.6) * mm, "end": v(0.86, 18.43) * mm});
            skLineSegment(sketch, "E150", {"start": v(0.86, 18.43) * mm, "end": v(1.5, 17.46) * mm});
            skLineSegment(sketch, "E151", {"start": v(1.5, 17.46) * mm, "end": v(1.96, 16.36) * mm});
            skLineSegment(sketch, "E152", {"start": v(1.96, 16.36) * mm, "end": v(2.02, 16.13) * mm});
            skLineSegment(sketch, "E153", {"start": v(2.02, 16.13) * mm, "end": v(2.06, 15.95) * mm});
            skLineSegment(sketch, "E154", {"start": v(2.06, 15.95) * mm, "end": v(2.26, 15.42) * mm});
            skLineSegment(sketch, "E155", {"start": v(2.26, 15.42) * mm, "end": v(2.62, 14.78) * mm});
            skLineSegment(sketch, "E156", {"start": v(2.62, 14.78) * mm, "end": v(3.08, 14.2) * mm});
            skLineSegment(sketch, "E157", {"start": v(3.08, 14.2) * mm, "end": v(3.48, 13.8) * mm});
            skLineSegment(sketch, "E158", {"start": v(3.48, 13.8) * mm, "end": v(3.62, 13.68) * mm});
            skLineSegment(sketch, "E159", {"start": v(3.62, 13.68) * mm, "end": v(3.46, 13.59) * mm});
            skLineSegment(sketch, "E160", {"start": v(3.46, 13.59) * mm, "end": v(2.95, 13.32) * mm});
            skLineSegment(sketch, "E161", {"start": v(2.95, 13.32) * mm, "end": v(2.27, 12.95) * mm});
            skLineSegment(sketch, "E162", {"start": v(2.27, 12.95) * mm, "end": v(1.64, 12.5) * mm});
            skLineSegment(sketch, "E163", {"start": v(1.64, 12.5) * mm, "end": v(1.21, 12.04) * mm});
            skLineSegment(sketch, "E164", {"start": v(1.21, 12.04) * mm, "end": v(1.1, 11.87) * mm});
            skLineSegment(sketch, "E165", {"start": v(1.1, 11.87) * mm, "end": v(1.04, 11.6) * mm});
            skLineSegment(sketch, "E166", {"start": v(1.04, 11.6) * mm, "end": v(1.09, 10.35) * mm});
            skLineSegment(sketch, "E167", {"start": v(1.09, 10.35) * mm, "end": v(1.45, 9.26) * mm});
            skLineSegment(sketch, "E168", {"start": v(1.45, 9.26) * mm, "end": v(1.56, 9.05) * mm});
            skLineSegment(sketch, "E169", {"start": v(1.56, 9.05) * mm, "end": v(-0.02, 4.48) * mm});
            skLineSegment(sketch, "E170", {"start": v(23.07, 26.26) * mm, "end": v(9.98, 24.62) * mm});
            skLineSegment(sketch, "E171", {"start": v(9.98, 24.62) * mm, "end": v(10, 24.54) * mm});
            skLineSegment(sketch, "E172", {"start": v(10, 24.54) * mm, "end": v(10.04, 24.3) * mm});
            skLineSegment(sketch, "E173", {"start": v(10.04, 24.3) * mm, "end": v(10.08, 23.95) * mm});
            skLineSegment(sketch, "E174", {"start": v(10.08, 23.95) * mm, "end": v(10.07, 23.57) * mm});
            skLineSegment(sketch, "E175", {"start": v(10.07, 23.57) * mm, "end": v(10, 23.23) * mm});
            skLineSegment(sketch, "E176", {"start": v(10, 23.23) * mm, "end": v(9.98, 23.12) * mm});
            skLineSegment(sketch, "E177", {"start": v(9.98, 23.12) * mm, "end": v(21.9, 22.01) * mm});
            skLineSegment(sketch, "E178", {"start": v(21.9, 22.01) * mm, "end": v(19.5, 17.32) * mm});
            skLineSegment(sketch, "E179", {"start": v(19.5, 17.32) * mm, "end": v(9.79, 21) * mm});
            skLineSegment(sketch, "E180", {"start": v(9.79, 21) * mm, "end": v(9.76, 20.87) * mm});
            skLineSegment(sketch, "E181", {"start": v(9.76, 20.87) * mm, "end": v(9.56, 20.27) * mm});
            skLineSegment(sketch, "E182", {"start": v(9.56, 20.27) * mm, "end": v(9.28, 19.74) * mm});
            skLineSegment(sketch, "E183", {"start": v(9.28, 19.74) * mm, "end": v(9.2, 19.64) * mm});
            skLineSegment(sketch, "E184", {"start": v(9.2, 19.64) * mm, "end": v(16.64, 14.14) * mm});
            skLineSegment(sketch, "E185", {"start": v(16.64, 14.14) * mm, "end": v(13.21, 11.82) * mm});
            skLineSegment(sketch, "E186", {"start": v(13.21, 11.82) * mm, "end": v(8.2, 17.86) * mm});
            skLineSegment(sketch, "E187", {"start": v(8.2, 17.86) * mm, "end": v(8.13, 17.8) * mm});
            skLineSegment(sketch, "E188", {"start": v(8.13, 17.8) * mm, "end": v(7.96, 17.6) * mm});
            skLineSegment(sketch, "E189", {"start": v(7.96, 17.6) * mm, "end": v(7.72, 17.35) * mm});
            skLineSegment(sketch, "E190", {"start": v(7.72, 17.35) * mm, "end": v(7.43, 17.12) * mm});
            skLineSegment(sketch, "E191", {"start": v(7.43, 17.12) * mm, "end": v(7.13, 16.97) * mm});
            skLineSegment(sketch, "E192", {"start": v(7.13, 16.97) * mm, "end": v(7.03, 16.94) * mm});
            skLineSegment(sketch, "E193", {"start": v(7.03, 16.94) * mm, "end": v(9.74, 10.9) * mm});
            skLineSegment(sketch, "E194", {"start": v(9.74, 10.9) * mm, "end": v(6.5, 10.18) * mm});
            skLineSegment(sketch, "E195", {"start": v(6.5, 10.18) * mm, "end": v(5.39, 15.92) * mm});
            skLineSegment(sketch, "E196", {"start": v(5.39, 15.92) * mm, "end": v(5.2, 15.86) * mm});
            skLineSegment(sketch, "E197", {"start": v(5.2, 15.86) * mm, "end": v(4.62, 15.79) * mm});
            skLineSegment(sketch, "E198", {"start": v(4.62, 15.79) * mm, "end": v(3.96, 15.95) * mm});
            skLineSegment(sketch, "E199", {"start": v(3.96, 15.95) * mm, "end": v(3.44, 16.32) * mm});
            skLineSegment(sketch, "E200", {"start": v(3.44, 16.32) * mm, "end": v(3.08, 16.85) * mm});
            skLineSegment(sketch, "E201", {"start": v(3.08, 16.85) * mm, "end": v(2.92, 17.45) * mm});
            skLineSegment(sketch, "E202", {"start": v(2.92, 17.45) * mm, "end": v(3, 18.05) * mm});
            skLineSegment(sketch, "E203", {"start": v(3, 18.05) * mm, "end": v(3.32, 18.58) * mm});
            skLineSegment(sketch, "E204", {"start": v(3.32, 18.58) * mm, "end": v(3.77, 18.9) * mm});
            skLineSegment(sketch, "E205", {"start": v(3.77, 18.9) * mm, "end": v(3.94, 18.97) * mm});
            skLineSegment(sketch, "E206", {"start": v(3.94, 18.97) * mm, "end": v(4.32, 19.1) * mm});
            skLineSegment(sketch, "E207", {"start": v(4.32, 19.1) * mm, "end": v(5.4, 19.6) * mm});
            skLineSegment(sketch, "E208", {"start": v(5.4, 19.6) * mm, "end": v(6.57, 20.42) * mm});
            skLineSegment(sketch, "E209", {"start": v(6.57, 20.42) * mm, "end": v(7.43, 21.44) * mm});
            skLineSegment(sketch, "E210", {"start": v(7.43, 21.44) * mm, "end": v(7.98, 22.66) * mm});
            skLineSegment(sketch, "E211", {"start": v(7.98, 22.66) * mm, "end": v(8.21, 24.08) * mm});
            skLineSegment(sketch, "E212", {"start": v(8.21, 24.08) * mm, "end": v(8.1, 25.73) * mm});
            skLineSegment(sketch, "E213", {"start": v(8.1, 25.73) * mm, "end": v(7.65, 27.6) * mm});
            skLineSegment(sketch, "E214", {"start": v(7.65, 27.6) * mm, "end": v(7.07, 29.18) * mm});
            skLineSegment(sketch, "E215", {"start": v(7.07, 29.18) * mm, "end": v(6.84, 29.7) * mm});
            skLineSegment(sketch, "E216", {"start": v(6.84, 29.7) * mm, "end": v(7.07, 29.52) * mm});
            skLineSegment(sketch, "E217", {"start": v(7.07, 29.52) * mm, "end": v(8.16, 28.5) * mm});
            skLineSegment(sketch, "E218", {"start": v(8.16, 28.5) * mm, "end": v(9.17, 27.03) * mm});
            skLineSegment(sketch, "E219", {"start": v(9.17, 27.03) * mm, "end": v(9.35, 26.65) * mm});
            skLineSegment(sketch, "E220", {"start": v(9.35, 26.65) * mm, "end": v(25.05, 32.35) * mm});
            skLineSegment(sketch, "E221", {"start": v(25.05, 32.35) * mm, "end": v(23.07, 26.26) * mm});
            skLineSegment(sketch, "E222", {"start": v(5.02, 5.2) * mm, "end": v(4.54, 6.82) * mm});
            skLineSegment(sketch, "E223", {"start": v(4.54, 6.82) * mm, "end": v(7.39, 6.82) * mm});
            skLineSegment(sketch, "E224", {"start": v(7.39, 6.82) * mm, "end": v(6.57, 4.62) * mm});
            skLineSegment(sketch, "E225", {"start": v(6.57, 4.62) * mm, "end": v(9.51, 6.94) * mm});
            skLineSegment(sketch, "E226", {"start": v(9.51, 6.94) * mm, "end": v(9.6, 7.01) * mm});
            skLineSegment(sketch, "E227", {"start": v(9.6, 7.01) * mm, "end": v(9.84, 7.28) * mm});
            skLineSegment(sketch, "E228", {"start": v(9.84, 7.28) * mm, "end": v(9.94, 7.58) * mm});
            skLineSegment(sketch, "E229", {"start": v(9.94, 7.58) * mm, "end": v(9.79, 7.79) * mm});
            skLineSegment(sketch, "E230", {"start": v(9.79, 7.79) * mm, "end": v(9.47, 7.86) * mm});
            skLineSegment(sketch, "E231", {"start": v(9.47, 7.86) * mm, "end": v(9.37, 7.86) * mm});
            skLineSegment(sketch, "E232", {"start": v(9.37, 7.86) * mm, "end": v(5.55, 7.86) * mm});
            skLineSegment(sketch, "E233", {"start": v(5.55, 7.86) * mm, "end": v(4.06, 11.14) * mm});
            skLineSegment(sketch, "E234", {"start": v(4.06, 11.14) * mm, "end": v(4.01, 11.22) * mm});
            skLineSegment(sketch, "E235", {"start": v(4.01, 11.22) * mm, "end": v(3.83, 11.44) * mm});
            skLineSegment(sketch, "E236", {"start": v(3.83, 11.44) * mm, "end": v(3.53, 11.6) * mm});
            skLineSegment(sketch, "E237", {"start": v(3.53, 11.6) * mm, "end": v(3.2, 11.64) * mm});
            skLineSegment(sketch, "E238", {"start": v(3.2, 11.64) * mm, "end": v(2.88, 11.56) * mm});
            skLineSegment(sketch, "E239", {"start": v(2.88, 11.56) * mm, "end": v(2.6, 11.39) * mm});
            skLineSegment(sketch, "E240", {"start": v(2.6, 11.39) * mm, "end": v(2.43, 11.12) * mm});
            skLineSegment(sketch, "E241", {"start": v(2.43, 11.12) * mm, "end": v(2.38, 10.78) * mm});
            skLineSegment(sketch, "E242", {"start": v(2.38, 10.78) * mm, "end": v(2.46, 10.46) * mm});
            skLineSegment(sketch, "E243", {"start": v(2.46, 10.46) * mm, "end": v(2.5, 10.37) * mm});
            skLineSegment(sketch, "E244", {"start": v(2.5, 10.37) * mm, "end": v(4.1, 7.86) * mm});
            skLineSegment(sketch, "E245", {"start": v(4.1, 7.86) * mm, "end": v(3.38, 7.86) * mm});
            skLineSegment(sketch, "E246", {"start": v(3.38, 7.86) * mm, "end": v(3.29, 7.86) * mm});
            skLineSegment(sketch, "E247", {"start": v(3.29, 7.86) * mm, "end": v(3.02, 7.77) * mm});
            skLineSegment(sketch, "E248", {"start": v(3.02, 7.77) * mm, "end": v(2.86, 7.54) * mm});
            skLineSegment(sketch, "E249", {"start": v(2.86, 7.54) * mm, "end": v(2.9, 7.24) * mm});
            skLineSegment(sketch, "E250", {"start": v(2.9, 7.24) * mm, "end": v(3.03, 7) * mm});
            skLineSegment(sketch, "E251", {"start": v(3.03, 7) * mm, "end": v(3.09, 6.94) * mm});
            skLineSegment(sketch, "E252", {"start": v(3.09, 6.94) * mm, "end": v(5.02, 5.2) * mm});
            skLineSegment(sketch, "E253", {"start": v(0, 35.47) * mm, "end": v(-3.8, 28.88) * mm});
            skLineSegment(sketch, "E254", {"start": v(-7.6, 22.3) * mm, "end": v(-3.8, 28.88) * mm});
            skLineSegment(sketch, "E255", {"start": v(-3.8, 28.88) * mm, "end": v(7.6, 22.3) * mm, "construction": true});
            skLineSegment(sketch, "E256", {"start": v(0, 35.47) * mm, "end": v(0, 22.3) * mm, "construction": true});
            skLineSegment(sketch, "E257", {"start": v(-7.6, 22.3) * mm, "end": v(3.8, 28.88) * mm, "construction": true});
            skLineSegment(sketch, "E258", {"start": v(-3.83, 28.9) * mm, "end": v(3.83, 28.9) * mm});
            skLineSegment(sketch, "E259", {"start": v(3.83, 28.9) * mm, "end": v(0, 22.27) * mm});
            skLineSegment(sketch, "E260", {"start": v(0, 22.27) * mm, "end": v(-3.83, 28.9) * mm});
            skSolve(sketch);
        }
        {
            var Q0;
            Q0=makeQuery(id+"F16.imprint","IMPRINT",FACE,{"disambiguationData":[TD([[makeQuery(id+"F16.imprint","IMPRINT",EDGE,{"derivedFrom":sQuery(id+"F16.wireOp",EDGE,"E86")}),1.0]])]});
            var Q1;
            Q1=makeQuery(id+"F16.imprint","IMPRINT",FACE,{"disambiguationData":[TD([[makeQuery(id+"F16.imprint","IMPRINT",EDGE,{"derivedFrom":sQuery(id+"F16.wireOp",EDGE,"E87")}),1.0]])]});
            var Q2;
            Q2=makeQuery(id+"F16.imprint","IMPRINT",FACE,{"disambiguationData":[TD([[makeQuery(id+"F16.imprint","IMPRINT",EDGE,{"derivedFrom":sQuery(id+"F16.wireOp",EDGE,"E89")}),1.0]])]});
            var Q3;
            Q3=makeQuery(id+"F16.imprint","IMPRINT",FACE,{"disambiguationData":[TD([[makeQuery(id+"F16.imprint","IMPRINT",EDGE,{"derivedFrom":sQuery(id+"F16.wireOp",EDGE,"E88")}),1.0]])]});
            var Q4;
            Q4=makeQuery(id+"F16.imprint","IMPRINT",FACE,{"disambiguationData":[TD([[makeQuery(id+"F16.imprint","IMPRINT",EDGE,{"derivedFrom":sQuery(id+"F16.wireOp",EDGE,"E221")}),-1.0]])]});
            var Q5;
            Q5=makeQuery(id+"F16.imprint","IMPRINT",FACE,{"disambiguationData":[TD([[makeQuery(id+"F16.imprint","IMPRINT",EDGE,{"derivedFrom":sQuery(id+"F16.wireOp",EDGE,"E122")}),-1.0]])]});
            var Q6;
            Q6=makeQuery(id+"F16.imprint","IMPRINT",FACE,{"disambiguationData":[TD([[makeQuery(id+"F16.imprint","IMPRINT",EDGE,{"derivedFrom":sQuery(id+"F16.wireOp",EDGE,"E222")}),1.0]])]});
            var Q7;
            Q7=makeQuery(id+"F16.imprint","IMPRINT",FACE,{"disambiguationData":[TD([[makeQuery(id+"F16.imprint","IMPRINT",EDGE,{"derivedFrom":sQuery(id+"F16.wireOp",EDGE,"E91")}),-1.0]])]});
            var Q8;
            Q8=makeQuery(id+"F16.imprint","IMPRINT",FACE,{"disambiguationData":[TD([[makeQuery(id+"F16.imprint","IMPRINT",EDGE,{"derivedFrom":sQuery(id+"F16.wireOp",EDGE,"E86")}),1.0]])]});
            var Q9;
            Q9=makeQuery(id+"F16.imprint","IMPRINT",FACE,{"disambiguationData":[TD([[makeQuery(id+"F16.imprint","IMPRINT",EDGE,{"derivedFrom":sQuery(id+"F16.wireOp",EDGE,"E87")}),1.0]])]});
            var Q10;
            Q10=makeQuery(id+"F16.imprint","IMPRINT",FACE,{"disambiguationData":[TD([[makeQuery(id+"F16.imprint","IMPRINT",EDGE,{"derivedFrom":sQuery(id+"F16.wireOp",EDGE,"E88")}),1.0]])]});
            var Q11;
            Q11=makeQuery(id+"F16.imprint","IMPRINT",FACE,{"disambiguationData":[TD([[makeQuery(id+"F16.imprint","IMPRINT",EDGE,{"derivedFrom":sQuery(id+"F16.wireOp",EDGE,"E89")}),1.0]])]});
            var Q12;
            Q12=makeQuery(id+"F16.imprint","IMPRINT",FACE,{"disambiguationData":[TD([[makeQuery(id+"F16.imprint","IMPRINT",EDGE,{"derivedFrom":sQuery(id+"F16.wireOp",EDGE,"E221")}),-1.0]])]});
            var Q13;
            Q13=makeQuery(id+"F16.imprint","IMPRINT",FACE,{"disambiguationData":[TD([[makeQuery(id+"F16.imprint","IMPRINT",EDGE,{"derivedFrom":sQuery(id+"F16.wireOp",EDGE,"E122")}),-1.0]])]});
            var Q14;
            Q14=makeQuery(id+"F16.imprint","IMPRINT",FACE,{"disambiguationData":[TD([[makeQuery(id+"F16.imprint","IMPRINT",EDGE,{"derivedFrom":sQuery(id+"F16.wireOp",EDGE,"E222")}),1.0]])]});
            var Q15;
            Q15=makeQuery(id+"F16.imprint","IMPRINT",FACE,{"disambiguationData":[TD([[makeQuery(id+"F16.imprint","IMPRINT",EDGE,{"derivedFrom":sQuery(id+"F16.wireOp",EDGE,"E91")}),-1.0]])]});
            var Q16;
            Q16=makeQuery(id+"F16.imprint","IMPRINT",FACE,{"disambiguationData":[TD([[makeQuery(id+"F16.imprint","IMPRINT",EDGE,{"derivedFrom":sQuery(id+"F16.wireOp",EDGE,"E86")}),1.0]])]});
            var Q17;
            Q17=makeQuery(id+"F16.imprint","IMPRINT",FACE,{"disambiguationData":[TD([[makeQuery(id+"F16.imprint","IMPRINT",EDGE,{"derivedFrom":sQuery(id+"F16.wireOp",EDGE,"E87")}),1.0]])]});
            var Q18;
            Q18=makeQuery(id+"F16.imprint","IMPRINT",FACE,{"disambiguationData":[TD([[makeQuery(id+"F16.imprint","IMPRINT",EDGE,{"derivedFrom":sQuery(id+"F16.wireOp",EDGE,"E88")}),1.0]])]});
            var Q19;
            Q19=makeQuery(id+"F16.imprint","IMPRINT",FACE,{"disambiguationData":[TD([[makeQuery(id+"F16.imprint","IMPRINT",EDGE,{"derivedFrom":sQuery(id+"F16.wireOp",EDGE,"E89")}),1.0]])]});
            var Q20;
            Q20=makeQuery(id+"F16.imprint","IMPRINT",FACE,{"disambiguationData":[TD([[makeQuery(id+"F16.imprint","IMPRINT",EDGE,{"derivedFrom":sQuery(id+"F16.wireOp",EDGE,"E221")}),-1.0]])]});
            var Q21;
            Q21=makeQuery(id+"F16.imprint","IMPRINT",FACE,{"disambiguationData":[TD([[makeQuery(id+"F16.imprint","IMPRINT",EDGE,{"derivedFrom":sQuery(id+"F16.wireOp",EDGE,"E122")}),-1.0]])]});
            var Q22;
            Q22=makeQuery(id+"F16.imprint","IMPRINT",FACE,{"disambiguationData":[TD([[makeQuery(id+"F16.imprint","IMPRINT",EDGE,{"derivedFrom":sQuery(id+"F16.wireOp",EDGE,"E222")}),1.0]])]});
            var Q23;
            Q23=makeQuery(id+"F16.imprint","IMPRINT",FACE,{"disambiguationData":[TD([[makeQuery(id+"F16.imprint","IMPRINT",EDGE,{"derivedFrom":sQuery(id+"F16.wireOp",EDGE,"E91")}),-1.0]])]});
            var Q24;
            Q24=makeQuery(id+"F16.imprint","IMPRINT",FACE,{"disambiguationData":[TD([[makeQuery(id+"F16.imprint","IMPRINT",EDGE,{"derivedFrom":sQuery(id+"F16.wireOp",EDGE,"E86")}),1.0]])]});
            var Q25;
            Q25=makeQuery(id+"F16.imprint","IMPRINT",FACE,{"disambiguationData":[TD([[makeQuery(id+"F16.imprint","IMPRINT",EDGE,{"derivedFrom":sQuery(id+"F16.wireOp",EDGE,"E221")}),-1.0]])]});
            var Q26;
            Q26=makeQuery(id+"F16.imprint","IMPRINT",FACE,{"disambiguationData":[TD([[makeQuery(id+"F16.imprint","IMPRINT",EDGE,{"derivedFrom":sQuery(id+"F16.wireOp",EDGE,"E222")}),1.0]])]});
            var Q27;
            Q27=makeQuery(id+"F16.imprint","IMPRINT",FACE,{"disambiguationData":[TD([[makeQuery(id+"F16.imprint","IMPRINT",EDGE,{"derivedFrom":sQuery(id+"F16.wireOp",EDGE,"E91")}),-1.0]])]});
            var Q28;
            Q28=makeQuery(id+"F16.imprint","IMPRINT",FACE,{"disambiguationData":[TD([[makeQuery(id+"F16.imprint","IMPRINT",EDGE,{"derivedFrom":sQuery(id+"F16.wireOp",EDGE,"E122")}),-1.0]])]});
            var Q29;
            {var subQ0=sQuery(id+"F1.wireOp",EDGE,"E2.MirrorCS");var subQ1=sQuery(id+"F1.wireOp",EDGE,"E1");Q29=makeQuery(id+"F6.boolean.opBoolean","MERGE",FACE,{"derivedFrom":[makeQuery(id+"F3.opExtrude","SWEPT_FACE",FACE,{"disambiguationData":[OSD([subQ1,subQ0])]}),makeQuery(id+"F6.opExtrude","SWEPT_FACE",FACE,{"disambiguationData":[OSD([subQ1,subQ0])]})]});}
            extrude(context, id + "F17", {"entities" : qUnion([Q0, Q1, Q2, Q3, Q4, Q5, Q6, Q7, Q8, Q9, Q10, Q11, Q12, Q13, Q14, Q15, Q16, Q17, Q18, Q19, Q20, Q21, Q22, Q23, Q24, Q25, Q26, Q27, Q28]), "operationType" : NewBodyOperationType.REMOVE, "oppositeDirection" : true, "depth" : (getVariable(context, 'wall_thickness') / 2) * mm, "endBoundEntityFace" : qUnion([Q29]), "offsetDistance" : 25 * mm});
        }
    });
